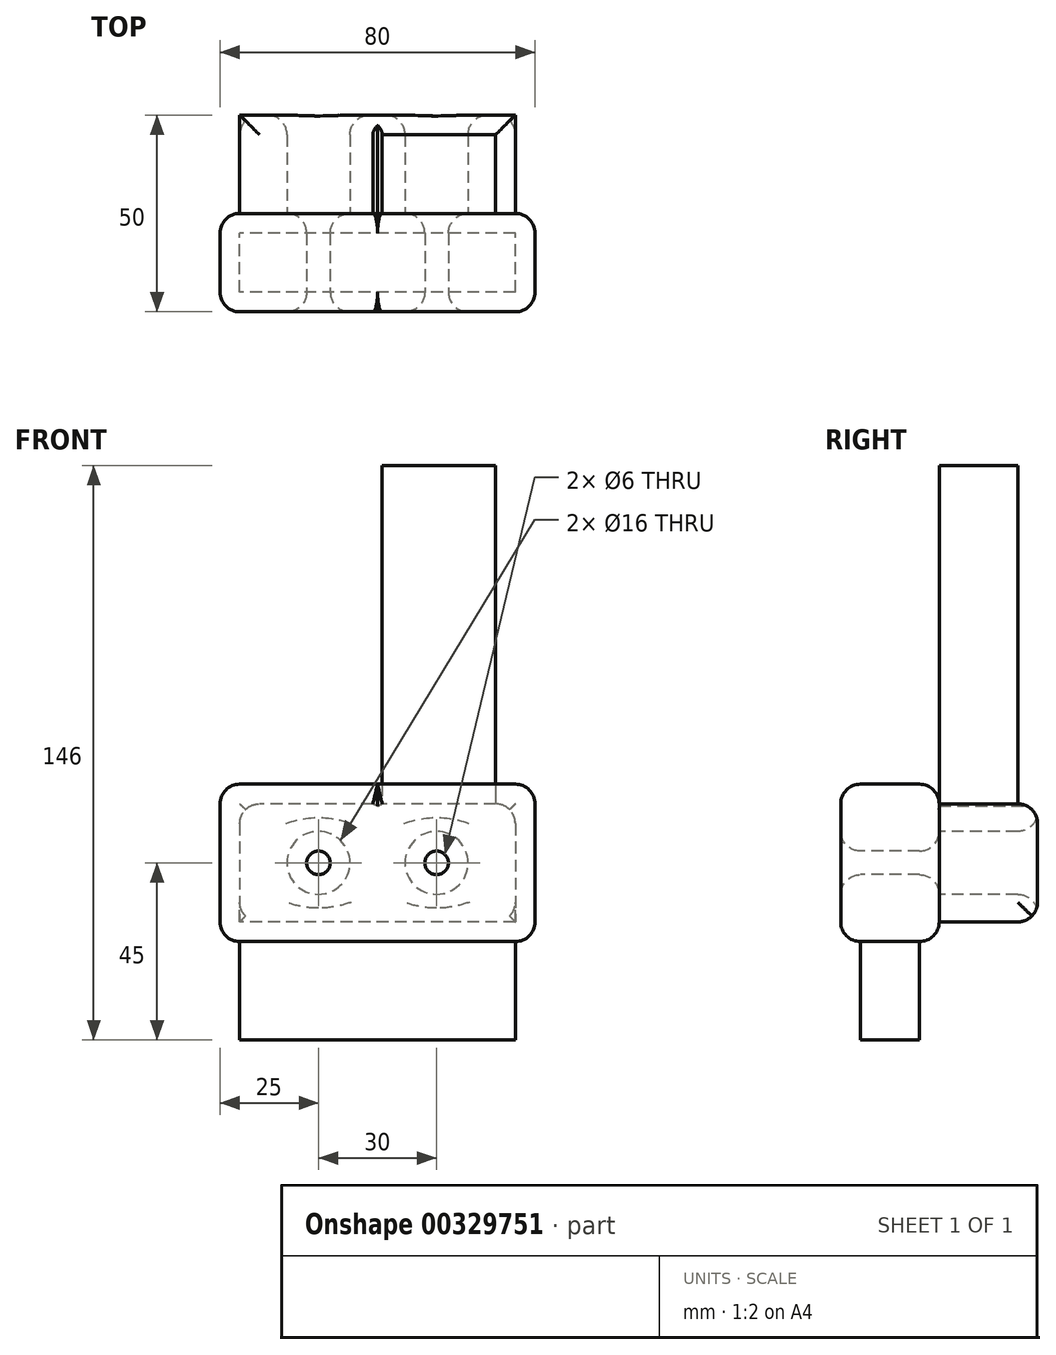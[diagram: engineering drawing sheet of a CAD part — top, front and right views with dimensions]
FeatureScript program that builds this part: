
annotation { "Feature Type Name" : "Feature", "Feature Type Description" : "" }
export const myFeature = defineFeature(function(context is Context, id is Id, definition is map)
    precondition{}
    {
        {
            var Q0;
            Q0=qCreatedBy(makeId("Front.planeOp"),FACE);
            var sketch = newSketch(context, id + "F0", { "sketchPlane" : qUnion([Q0])});
            skLineSegment(sketch, "E0.bottom", {"start": v(40, 20) * mm, "end": v(-40, 20) * mm});
            skLineSegment(sketch, "E0.top", {"start": v(40, -20) * mm, "end": v(-40, -20) * mm});
            skLineSegment(sketch, "E0.left", {"start": v(40, 20) * mm, "end": v(40, -20) * mm});
            skLineSegment(sketch, "E0.right", {"start": v(-40, 20) * mm, "end": v(-40, -20) * mm});
            skPoint(sketch, "E0.middle", {"position": v(0, 0) * mm});
            skSolve(sketch);
        }
        {
            var Q0;
            Q0 = qSketchRegion(id + "F0", true);
            extrude(context, id + "F1", {"entities" : qUnion([Q0]), "depth" : 25 * mm});
        }
        {
            var Q0;
            Q0=makeQuery(id+"F1.opExtrude","CAP_FACE",FACE,{"disambiguationData":[OSD([sQuery(id+"F0.wireOp",EDGE,"E0.bottom"),sQuery(id+"F0.wireOp",EDGE,"E0.top"),sQuery(id+"F0.wireOp",EDGE,"E0.left"),sQuery(id+"F0.wireOp",EDGE,"E0.right")])],"isStart":false});
            var sketch = newSketch(context, id + "F2", { "sketchPlane" : qUnion([Q0])});
            skLineSegment(sketch, "E1", {"start": v(0, 0) * mm, "end": v(15, 0) * mm});
            skLineSegment(sketch, "E2", {"start": v(15, 0) * mm, "end": v(0, 0) * mm});
            skLineSegment(sketch, "E3", {"start": v(-15, 0) * mm, "end": v(0, 0) * mm});
            skCircle(sketch, "E4", {"center": v(-15, 0) * mm, "radius": 3 * mm});
            skCircle(sketch, "E5", {"center": v(15, 0) * mm, "radius": 3 * mm});
            skSolve(sketch);
        }
        {
            var Q0;
            Q0=makeQuery(id+"F2.imprint","IMPRINT",FACE,{"disambiguationData":[TD([[makeQuery(id+"F2.imprint","IMPRINT",EDGE,{"derivedFrom":sQuery(id+"F2.wireOp",EDGE,"E4")}),1.0]])]});
            var Q1;
            Q1=makeQuery(id+"F2.imprint","IMPRINT",FACE,{"disambiguationData":[TD([[makeQuery(id+"F2.imprint","IMPRINT",EDGE,{"derivedFrom":sQuery(id+"F2.wireOp",EDGE,"E5")}),1.0]])]});
            extrude(context, id + "F3", {"entities" : qUnion([Q0, Q1]), "operationType" : NewBodyOperationType.REMOVE, "oppositeDirection" : true, "depth" : 25 * mm});
        }
        {
            var Q0;
            Q0=makeQuery(id+"F1.opExtrude","CAP_FACE",FACE,{"disambiguationData":[OSD([sQuery(id+"F0.wireOp",EDGE,"E0.bottom"),sQuery(id+"F0.wireOp",EDGE,"E0.top"),sQuery(id+"F0.wireOp",EDGE,"E0.left"),sQuery(id+"F0.wireOp",EDGE,"E0.right")])],"isStart":false});
            var sketch = newSketch(context, id + "F4", { "sketchPlane" : qUnion([Q0])});
            skLineSegment(sketch, "E6", {"start": v(0, 20) * mm, "end": v(-40, 0) * mm});
            skLineSegment(sketch, "E7", {"start": v(-40, 0) * mm, "end": v(-40, 20) * mm});
            skLineSegment(sketch, "E8", {"start": v(-40, 20) * mm, "end": v(0, 20) * mm});
            skSolve(sketch);
        }
        {
            var Q0;
            Q0 = qSketchRegion(id + "F4", true);
            extrude(context, id + "F5", {"entities" : qUnion([Q0]), "operationType" : NewBodyOperationType.REMOVE, "oppositeDirection" : true, "depth" : 25 * mm});
        }
        {
            var Q0;
            Q0=makeQuery(id+"F1.opExtrude","CAP_FACE",FACE,{"disambiguationData":[OSD([sQuery(id+"F0.wireOp",EDGE,"E0.bottom"),sQuery(id+"F0.wireOp",EDGE,"E0.top"),sQuery(id+"F0.wireOp",EDGE,"E0.left"),sQuery(id+"F0.wireOp",EDGE,"E0.right")])],"isStart":false});
            fillet(context, id + "F6", {"entities" : qUnion([Q0]), "radius" : 5 * mm, "tangentPropagation" : true, "allowEdgeOverflow" : false});
        }
        {
            var Q0;
            Q0=makeQuery(id+"F1.opExtrude","CAP_FACE",FACE,{"disambiguationData":[OSD([sQuery(id+"F0.wireOp",EDGE,"E0.bottom"),sQuery(id+"F0.wireOp",EDGE,"E0.top"),sQuery(id+"F0.wireOp",EDGE,"E0.left"),sQuery(id+"F0.wireOp",EDGE,"E0.right")])],"isStart":true});
            fillet(context, id + "F7", {"entities" : qUnion([Q0]), "radius" : 5 * mm, "tangentPropagation" : true, "allowEdgeOverflow" : false});
        }
        {
            var Q0;
            Q0=makeQuery(id+"F1.opExtrude","SWEPT_FACE",FACE,{"disambiguationData":[OSD([sQuery(id+"F0.wireOp",EDGE,"E0.right")])]});
            var Q1;
            Q1=makeQuery(id+"F7.opFillet","BLEND_EDGE",EDGE,{"blendedFrom":[makeQuery(id+"F5.boolean.opBoolean","COPY",EDGE,{"derivedFrom":makeQuery(id+"F5.opExtrude","CAP_EDGE",EDGE,{"disambiguationData":[OSD([sQuery(id+"F4.wireOp",EDGE,"E6")])],"isStart":false})}),makeQuery(id+"F1.opExtrude","CAP_EDGE",EDGE,{"disambiguationData":[OSD([sQuery(id+"F0.wireOp",EDGE,"E0.right")])],"isStart":true})],"blendedInto":[]});
            var Q2;
            Q2=makeQuery(id+"F6.opFillet","BLEND_EDGE",EDGE,{"blendedFrom":[makeQuery(id+"F5.boolean.opBoolean","COPY",EDGE,{"derivedFrom":makeQuery(id+"F5.opExtrude","CAP_EDGE",EDGE,{"disambiguationData":[OSD([sQuery(id+"F4.wireOp",EDGE,"E6")])],"isStart":true})}),makeQuery(id+"F1.opExtrude","CAP_EDGE",EDGE,{"disambiguationData":[OSD([sQuery(id+"F0.wireOp",EDGE,"E0.right")])],"isStart":false})],"blendedInto":[]});
            var Q3;
            Q3=makeQuery(id+"F5.boolean.opBoolean","COPY",EDGE,{"derivedFrom":makeQuery(id+"F5.opExtrude","SWEPT_EDGE",EDGE,{"disambiguationData":[OSD([sQuery(id+"F0.wireOp",EDGE,"E0.bottom"),sQuery(id+"F4.wireOp",EDGE,"E6"),sQuery(id+"F4.wireOp",EDGE,"E8")])]})});
            fillet(context, id + "F8", {"entities" : qUnion([Q0, Q1, Q2, Q3]), "radius" : 5 * mm, "tangentPropagation" : true, "allowEdgeOverflow" : false});
        }
        {
            var Q0;
            Q0=makeQuery(id+"F1.opExtrude","SWEPT_EDGE",EDGE,{"disambiguationData":[OSD([sQuery(id+"F0.wireOp",EDGE,"E0.top"),sQuery(id+"F0.wireOp",EDGE,"E0.left")])]});
            var Q1;
            Q1=makeQuery(id+"F7.opFillet","BLEND_EDGE",EDGE,{"blendedFrom":[makeQuery(id+"F1.opExtrude","CAP_EDGE",EDGE,{"disambiguationData":[OSD([sQuery(id+"F0.wireOp",EDGE,"E0.top")])],"isStart":true}),makeQuery(id+"F1.opExtrude","CAP_EDGE",EDGE,{"disambiguationData":[OSD([sQuery(id+"F0.wireOp",EDGE,"E0.left")])],"isStart":true})],"blendedInto":[]});
            var Q2;
            Q2=makeQuery(id+"F1.opExtrude","SWEPT_EDGE",EDGE,{"disambiguationData":[OSD([sQuery(id+"F0.wireOp",EDGE,"E0.bottom"),sQuery(id+"F0.wireOp",EDGE,"E0.left")])]});
            fillet(context, id + "F9", {"entities" : qUnion([Q0, Q1, Q2]), "radius" : 5 * mm, "tangentPropagation" : true, "allowEdgeOverflow" : false});
        }
        {
            var Q0;
            Q0=makeQuery(id+"F1.opExtrude","CAP_FACE",FACE,{"disambiguationData":[OSD([sQuery(id+"F0.wireOp",EDGE,"E0.bottom"),sQuery(id+"F0.wireOp",EDGE,"E0.top"),sQuery(id+"F0.wireOp",EDGE,"E0.left"),sQuery(id+"F0.wireOp",EDGE,"E0.right")])],"isStart":true});
            extrude(context, id + "F10", {"entities" : qUnion([Q0]), "operationType" : NewBodyOperationType.ADD, "depth" : 25 * mm});
        }
        {
            var Q0;
            {var subQ0=sQuery(id+"F0.wireOp",EDGE,"E0.right");var subQ1=sQuery(id+"F0.wireOp",EDGE,"E0.left");var subQ2=sQuery(id+"F0.wireOp",EDGE,"E0.top");var subQ3=sQuery(id+"F0.wireOp",EDGE,"E0.bottom");Q0=makeQuery(id+"F10.opExtrude","CAP_EDGE",EDGE,{"disambiguationData":[OSD([subQ3,subQ2,subQ1,subQ0]),TDD([makeQuery(id+"F7.opFillet","BLEND_EDGE",EDGE,{"blendedFrom":[makeQuery(id+"F1.opExtrude","CAP_EDGE",EDGE,{"disambiguationData":[OSD([subQ3])],"isStart":true}),makeQuery(id+"F1.opExtrude","CAP_FACE",FACE,{"disambiguationData":[OSD([subQ3,subQ2,subQ1,subQ0])],"isStart":true})],"blendedInto":[makeQuery(id+"F1.opExtrude","CAP_FACE",FACE,{"disambiguationData":[OSD([subQ3,subQ2,subQ1,subQ0])],"isStart":true})]})])],"isStart":false});}
            var Q1;
            {var subQ0=sQuery(id+"F0.wireOp",EDGE,"E0.right");var subQ1=sQuery(id+"F0.wireOp",EDGE,"E0.left");var subQ2=sQuery(id+"F0.wireOp",EDGE,"E0.top");var subQ3=sQuery(id+"F0.wireOp",EDGE,"E0.bottom");var subQ4=sQuery(id+"F4.wireOp",EDGE,"E6");Q1=makeQuery(id+"F10.opExtrude","CAP_EDGE",EDGE,{"disambiguationData":[OSD([subQ3,subQ2,subQ1,subQ0,subQ4]),TDD([makeQuery(id+"F7.opFillet","BLEND_EDGE",EDGE,{"disambiguationData":[OD(1.0)],"blendedFrom":[makeQuery(id+"F5.boolean.opBoolean","COPY",EDGE,{"derivedFrom":makeQuery(id+"F5.opExtrude","CAP_EDGE",EDGE,{"disambiguationData":[OSD([subQ4])],"isStart":false})}),makeQuery(id+"F1.opExtrude","CAP_FACE",FACE,{"disambiguationData":[OSD([subQ3,subQ2,subQ1,subQ0])],"isStart":true})],"blendedInto":[makeQuery(id+"F1.opExtrude","CAP_FACE",FACE,{"disambiguationData":[OSD([subQ3,subQ2,subQ1,subQ0])],"isStart":true})]})])],"isStart":false});}
            var Q2;
            {var subQ0=sQuery(id+"F0.wireOp",EDGE,"E0.right");var subQ1=sQuery(id+"F0.wireOp",EDGE,"E0.left");var subQ2=sQuery(id+"F0.wireOp",EDGE,"E0.top");var subQ3=sQuery(id+"F0.wireOp",EDGE,"E0.bottom");Q2=makeQuery(id+"F10.opExtrude","CAP_EDGE",EDGE,{"disambiguationData":[OSD([subQ3,subQ2,subQ1,subQ0]),TDD([makeQuery(id+"F7.opFillet","BLEND_EDGE",EDGE,{"blendedFrom":[makeQuery(id+"F1.opExtrude","CAP_EDGE",EDGE,{"disambiguationData":[OSD([subQ2])],"isStart":true}),makeQuery(id+"F1.opExtrude","CAP_FACE",FACE,{"disambiguationData":[OSD([subQ3,subQ2,subQ1,subQ0])],"isStart":true})],"blendedInto":[makeQuery(id+"F1.opExtrude","CAP_FACE",FACE,{"disambiguationData":[OSD([subQ3,subQ2,subQ1,subQ0])],"isStart":true})]})])],"isStart":false});}
            var Q3;
            {var subQ0=sQuery(id+"F0.wireOp",EDGE,"E0.bottom");var subQ1=sQuery(id+"F0.wireOp",EDGE,"E0.right");var subQ2=sQuery(id+"F0.wireOp",EDGE,"E0.left");var subQ3=sQuery(id+"F0.wireOp",EDGE,"E0.top");Q3=makeQuery(id+"F10.opExtrude","SWEPT_EDGE",EDGE,{"disambiguationData":[OSD([subQ0,subQ3,subQ2,subQ1]),TDD([makeQuery(id+"F9.opFillet","BLEND_VERTEX",VERTEX,{"blendedFrom":[makeQuery(id+"F7.opFillet","BLEND_EDGE",EDGE,{"blendedFrom":[makeQuery(id+"F1.opExtrude","CAP_EDGE",EDGE,{"disambiguationData":[OSD([subQ2])],"isStart":true}),makeQuery(id+"F1.opExtrude","CAP_EDGE",EDGE,{"disambiguationData":[OSD([subQ0])],"isStart":true})],"blendedInto":[]}),makeQuery(id+"F7.opFillet","BLEND_FACE",FACE,{"disambiguationData":[OSD([subQ2])]}),makeQuery(id+"F1.opExtrude","CAP_FACE",FACE,{"disambiguationData":[OSD([subQ0,subQ3,subQ2,subQ1])],"isStart":true}),makeQuery(id+"F7.opFillet","BLEND_FACE",FACE,{"disambiguationData":[OSD([subQ0])]})],"blendedInto":[makeQuery(id+"F7.opFillet","BLEND_FACE",FACE,{"disambiguationData":[OSD([subQ2])]}),makeQuery(id+"F1.opExtrude","CAP_FACE",FACE,{"disambiguationData":[OSD([subQ0,subQ3,subQ2,subQ1])],"isStart":true}),makeQuery(id+"F7.opFillet","BLEND_FACE",FACE,{"disambiguationData":[OSD([subQ0])]})]})])]});}
            var Q4;
            {var subQ0=sQuery(id+"F0.wireOp",EDGE,"E0.top");var subQ1=sQuery(id+"F0.wireOp",EDGE,"E0.right");var subQ2=sQuery(id+"F0.wireOp",EDGE,"E0.left");var subQ3=sQuery(id+"F0.wireOp",EDGE,"E0.bottom");Q4=makeQuery(id+"F10.opExtrude","SWEPT_EDGE",EDGE,{"disambiguationData":[OSD([subQ3,subQ0,subQ2,subQ1]),TDD([makeQuery(id+"F9.opFillet","BLEND_VERTEX",VERTEX,{"blendedFrom":[makeQuery(id+"F7.opFillet","BLEND_EDGE",EDGE,{"blendedFrom":[makeQuery(id+"F1.opExtrude","CAP_EDGE",EDGE,{"disambiguationData":[OSD([subQ0])],"isStart":true}),makeQuery(id+"F1.opExtrude","CAP_EDGE",EDGE,{"disambiguationData":[OSD([subQ2])],"isStart":true})],"blendedInto":[]}),makeQuery(id+"F7.opFillet","BLEND_FACE",FACE,{"disambiguationData":[OSD([subQ2])]}),makeQuery(id+"F1.opExtrude","CAP_FACE",FACE,{"disambiguationData":[OSD([subQ3,subQ0,subQ2,subQ1])],"isStart":true}),makeQuery(id+"F7.opFillet","BLEND_FACE",FACE,{"disambiguationData":[OSD([subQ0])]})],"blendedInto":[makeQuery(id+"F7.opFillet","BLEND_FACE",FACE,{"disambiguationData":[OSD([subQ2])]}),makeQuery(id+"F1.opExtrude","CAP_FACE",FACE,{"disambiguationData":[OSD([subQ3,subQ0,subQ2,subQ1])],"isStart":true}),makeQuery(id+"F7.opFillet","BLEND_FACE",FACE,{"disambiguationData":[OSD([subQ0])]})]})])]});}
            var Q5;
            {var subQ0=sQuery(id+"F0.wireOp",EDGE,"E0.right");var subQ1=sQuery(id+"F0.wireOp",EDGE,"E0.left");var subQ2=sQuery(id+"F0.wireOp",EDGE,"E0.top");var subQ3=sQuery(id+"F0.wireOp",EDGE,"E0.bottom");var subQ4=sQuery(id+"F4.wireOp",EDGE,"E6");Q5=makeQuery(id+"F10.opExtrude","SWEPT_EDGE",EDGE,{"disambiguationData":[OSD([subQ3,subQ2,subQ1,subQ0,subQ4]),TDD([makeQuery(id+"F8.opFillet","BLEND_VERTEX",VERTEX,{"blendedFrom":[makeQuery(id+"F7.opFillet","BLEND_EDGE",EDGE,{"blendedFrom":[makeQuery(id+"F5.boolean.opBoolean","COPY",EDGE,{"derivedFrom":makeQuery(id+"F5.opExtrude","CAP_EDGE",EDGE,{"disambiguationData":[OSD([subQ4])],"isStart":false})}),makeQuery(id+"F1.opExtrude","CAP_EDGE",EDGE,{"disambiguationData":[OSD([subQ0])],"isStart":true})],"blendedInto":[]}),makeQuery(id+"F7.opFillet","BLEND_FACE",FACE,{"disambiguationData":[OSD([subQ4])]}),makeQuery(id+"F7.opFillet","BLEND_FACE",FACE,{"disambiguationData":[OSD([subQ0])]}),makeQuery(id+"F1.opExtrude","CAP_FACE",FACE,{"disambiguationData":[OSD([subQ3,subQ2,subQ1,subQ0])],"isStart":true})],"blendedInto":[makeQuery(id+"F7.opFillet","BLEND_FACE",FACE,{"disambiguationData":[OSD([subQ4])]}),makeQuery(id+"F7.opFillet","BLEND_FACE",FACE,{"disambiguationData":[OSD([subQ0])]}),makeQuery(id+"F1.opExtrude","CAP_FACE",FACE,{"disambiguationData":[OSD([subQ3,subQ2,subQ1,subQ0])],"isStart":true})]})])]});}
            var Q6;
            {var subQ0=sQuery(id+"F0.wireOp",EDGE,"E0.right");var subQ1=sQuery(id+"F0.wireOp",EDGE,"E0.left");var subQ2=sQuery(id+"F0.wireOp",EDGE,"E0.top");var subQ3=sQuery(id+"F0.wireOp",EDGE,"E0.bottom");Q6=makeQuery(id+"F10.opExtrude","SWEPT_EDGE",EDGE,{"disambiguationData":[OSD([subQ3,subQ2,subQ1,subQ0]),TDD([makeQuery(id+"F7.opFillet","BLEND_VERTEX",VERTEX,{"blendedFrom":[makeQuery(id+"F1.opExtrude","CAP_EDGE",EDGE,{"disambiguationData":[OSD([subQ2])],"isStart":true}),makeQuery(id+"F1.opExtrude","CAP_EDGE",EDGE,{"disambiguationData":[OSD([subQ0])],"isStart":true}),makeQuery(id+"F1.opExtrude","CAP_FACE",FACE,{"disambiguationData":[OSD([subQ3,subQ2,subQ1,subQ0])],"isStart":true})],"blendedInto":[makeQuery(id+"F1.opExtrude","CAP_FACE",FACE,{"disambiguationData":[OSD([subQ3,subQ2,subQ1,subQ0])],"isStart":true})]})])]});}
            var Q7;
            {var subQ0=sQuery(id+"F0.wireOp",EDGE,"E0.right");var subQ1=sQuery(id+"F0.wireOp",EDGE,"E0.left");var subQ2=sQuery(id+"F0.wireOp",EDGE,"E0.top");var subQ3=sQuery(id+"F0.wireOp",EDGE,"E0.bottom");Q7=makeQuery(id+"F10.opExtrude","CAP_EDGE",EDGE,{"disambiguationData":[OSD([subQ3,subQ2,subQ1,subQ0]),TDD([makeQuery(id+"F7.opFillet","BLEND_EDGE",EDGE,{"blendedFrom":[makeQuery(id+"F1.opExtrude","CAP_EDGE",EDGE,{"disambiguationData":[OSD([subQ0])],"isStart":true}),makeQuery(id+"F1.opExtrude","CAP_FACE",FACE,{"disambiguationData":[OSD([subQ3,subQ2,subQ1,subQ0])],"isStart":true})],"blendedInto":[makeQuery(id+"F1.opExtrude","CAP_FACE",FACE,{"disambiguationData":[OSD([subQ3,subQ2,subQ1,subQ0])],"isStart":true})]})])],"isStart":false});}
            var Q8;
            Q8=makeQuery(id+"F10.opExtrude","CAP_EDGE",EDGE,{"disambiguationData":[OSD([sQuery(id+"F0.wireOp",EDGE,"E0.bottom"),sQuery(id+"F0.wireOp",EDGE,"E0.top"),sQuery(id+"F0.wireOp",EDGE,"E0.left"),sQuery(id+"F0.wireOp",EDGE,"E0.right"),sQuery(id+"F2.wireOp",EDGE,"E5")])],"isStart":false});
            var Q9;
            Q9=makeQuery(id+"F10.opExtrude","CAP_EDGE",EDGE,{"disambiguationData":[OSD([sQuery(id+"F0.wireOp",EDGE,"E0.bottom"),sQuery(id+"F0.wireOp",EDGE,"E0.top"),sQuery(id+"F0.wireOp",EDGE,"E0.left"),sQuery(id+"F0.wireOp",EDGE,"E0.right"),sQuery(id+"F2.wireOp",EDGE,"E4")])],"isStart":false});
            fillet(context, id + "F11", {"entities" : qUnion([Q0, Q1, Q2, Q3, Q4, Q5, Q6, Q7, Q8, Q9]), "radius" : 5 * mm, "tangentPropagation" : true, "allowEdgeOverflow" : false});
        }
        {
            var Q0;
            Q0=makeQuery(id+"F1.opExtrude","SWEPT_BODY",BODY,{"disambiguationData":[OSD([sQuery(id+"F0.wireOp",EDGE,"E0.bottom"),sQuery(id+"F0.wireOp",EDGE,"E0.top"),sQuery(id+"F0.wireOp",EDGE,"E0.left"),sQuery(id+"F0.wireOp",EDGE,"E0.right")])]});
            var Q1;
            Q1=qCreatedBy(makeId("Right.planeOp"),FACE);
            mirror(context, id + "F12", {"operationType" : NewBodyOperationType.ADD, "entities" : qUnion([Q0]), "mirrorPlane" : qUnion([Q1])});
        }
        {
            var Q0;
            {var subQ0=sQuery(id+"F0.wireOp",EDGE,"E0.right");var subQ1=sQuery(id+"F0.wireOp",EDGE,"E0.left");var subQ2=sQuery(id+"F0.wireOp",EDGE,"E0.top");var subQ3=sQuery(id+"F0.wireOp",EDGE,"E0.bottom");Q0=makeQuery(id+"F10.opExtrude","SWEPT_FACE",FACE,{"disambiguationData":[OSD([subQ3,subQ2,subQ1,subQ0]),TDD([makeQuery(id+"F7.opFillet","BLEND_EDGE",EDGE,{"blendedFrom":[makeQuery(id+"F1.opExtrude","CAP_EDGE",EDGE,{"disambiguationData":[OSD([subQ3])],"isStart":true}),makeQuery(id+"F1.opExtrude","CAP_FACE",FACE,{"disambiguationData":[OSD([subQ3,subQ2,subQ1,subQ0])],"isStart":true})],"blendedInto":[makeQuery(id+"F1.opExtrude","CAP_FACE",FACE,{"disambiguationData":[OSD([subQ3,subQ2,subQ1,subQ0])],"isStart":true})]})])]});}
            extrude(context, id + "F13", {"entities" : qUnion([Q0]), "operationType" : NewBodyOperationType.ADD, "depth" : 86 * mm});
        }
        {
            var Q0;
            Q0=makeQuery(id+"F1.opExtrude","SWEPT_FACE",FACE,{"disambiguationData":[OSD([sQuery(id+"F0.wireOp",EDGE,"E0.top")])]});
            extrude(context, id + "F14", {"entities" : qUnion([Q0]), "operationType" : NewBodyOperationType.ADD, "depth" : 25 * mm});
        }
    });
